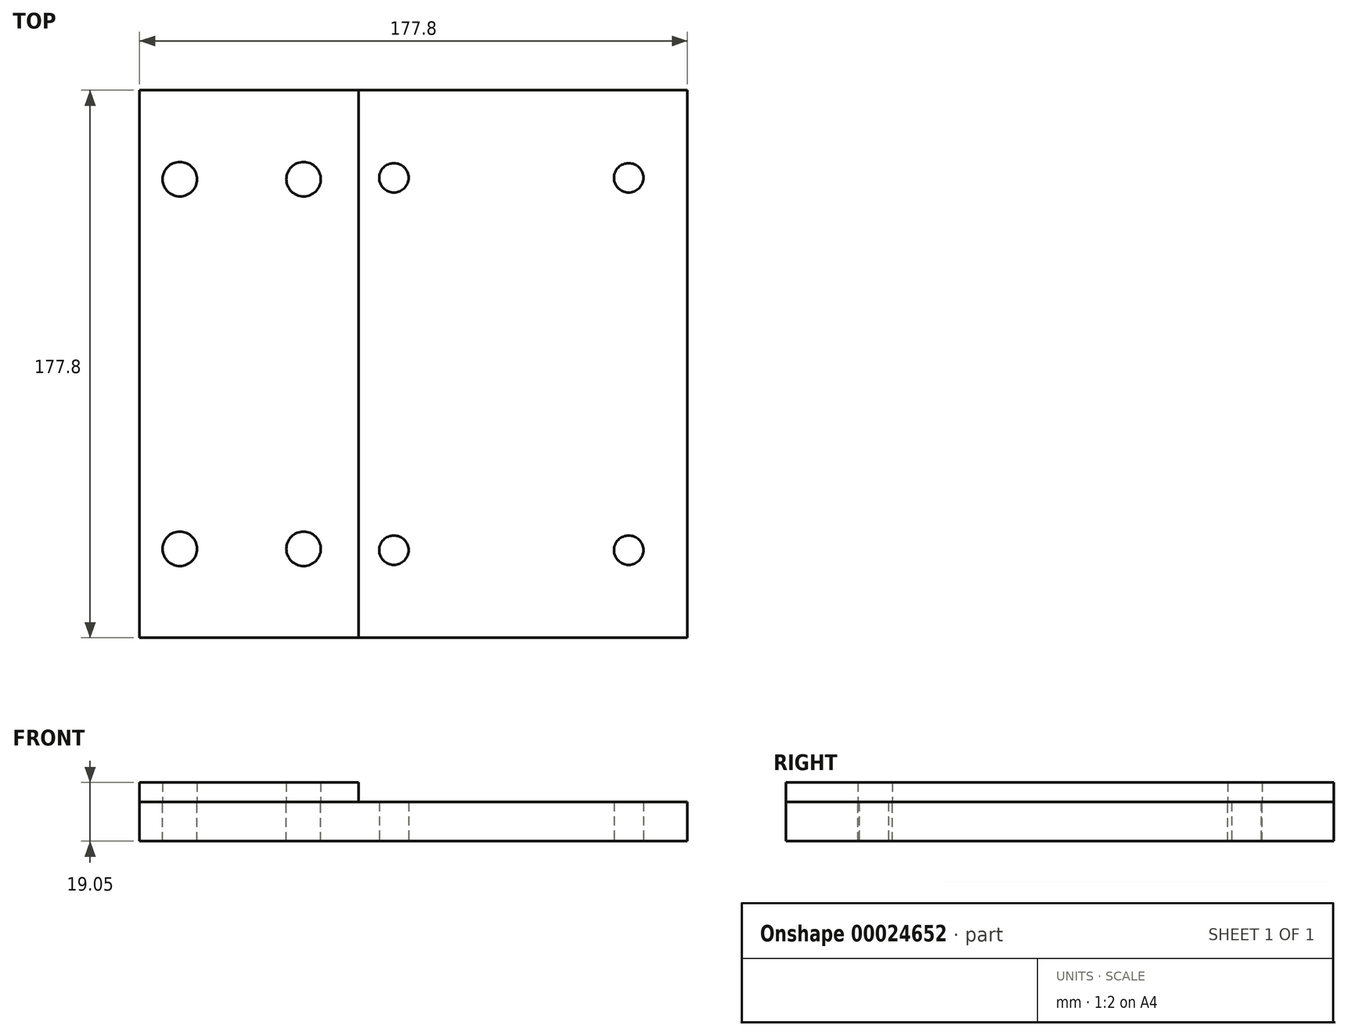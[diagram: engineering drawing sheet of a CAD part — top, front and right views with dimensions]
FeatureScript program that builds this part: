
annotation { "Feature Type Name" : "Feature", "Feature Type Description" : "" }
export const myFeature = defineFeature(function(context is Context, id is Id, definition is map)
    precondition{}
    {
        {
            var Q0;
            Q0=qCreatedBy(makeId("Top.planeOp"),FACE);
            var sketch = newSketch(context, id + "F0", { "sketchPlane" : qUnion([Q0])});
            skLineSegment(sketch, "E0.rect.bottom", {"start": v(-88.9, 88.9) * mm, "end": v(88.9, 88.9) * mm});
            skLineSegment(sketch, "E0.rect.top", {"start": v(-88.9, -88.9) * mm, "end": v(88.9, -88.9) * mm});
            skLineSegment(sketch, "E0.rect.left", {"start": v(-88.9, 88.9) * mm, "end": v(-88.9, -88.9) * mm});
            skLineSegment(sketch, "E0.rect.right", {"start": v(88.9, 88.9) * mm, "end": v(88.9, -88.9) * mm});
            skPoint(sketch, "E0.rect.middle", {"position": v(0, 0) * mm});
            skLineSegment(sketch, "E1.0", {"start": v(31.75, 88.9) * mm, "end": v(31.75, -88.9) * mm, "construction": true});
            skLineSegment(sketch, "E2.0", {"start": v(69.85, 88.9) * mm, "end": v(69.85, -88.9) * mm, "construction": true});
            skLineSegment(sketch, "E3", {"start": v(0, 0) * mm, "end": v(100.51, 0) * mm, "construction": true});
            skLineSegment(sketch, "E4.0", {"start": v(0, 60.45) * mm, "end": v(100.51, 60.45) * mm, "construction": true});
            skCircle(sketch, "E5", {"center": v(69.85, 60.45) * mm, "radius": 4.76 * mm});
            skCircle(sketch, "E6.MirrorC", {"center": v(-6.35, 60.45) * mm, "radius": 4.76 * mm});
            skCircle(sketch, "E7.MirrorC", {"center": v(-6.35, -60.45) * mm, "radius": 4.76 * mm});
            skCircle(sketch, "E8.MirrorC", {"center": v(69.85, -60.45) * mm, "radius": 4.76 * mm});
            skSolve(sketch);
        }
        {
            var Q0;
            Q0=makeQuery(id+"F0.imprint","IMPRINT",FACE,{"disambiguationData":[TD([[makeQuery(id+"F0.imprint","IMPRINT",EDGE,{"derivedFrom":sQuery(id+"F0.wireOp",EDGE,"E0.rect.bottom")}),-1.0]])]});
            extrude(context, id + "F1", {"entities" : qUnion([Q0]), "depth" : 12.7 * mm});
        }
        {
            var Q0;
            Q0=makeQuery(id+"F1.opExtrude","CAP_FACE",FACE,{"disambiguationData":[OSD([sQuery(id+"F0.wireOp",EDGE,"E0.rect.bottom"),sQuery(id+"F0.wireOp",EDGE,"E0.rect.top"),sQuery(id+"F0.wireOp",EDGE,"E0.rect.left"),sQuery(id+"F0.wireOp",EDGE,"E0.rect.right"),sQuery(id+"F0.wireOp",EDGE,"E5"),sQuery(id+"F0.wireOp",EDGE,"E6.MirrorC"),sQuery(id+"F0.wireOp",EDGE,"E7.MirrorC"),sQuery(id+"F0.wireOp",EDGE,"E8.MirrorC")])],"isStart":false});
            var sketch = newSketch(context, id + "F2", { "sketchPlane" : qUnion([Q0])});
            skLineSegment(sketch, "E9", {"start": v(-88.9, 0) * mm, "end": v(102.79, 0) * mm, "construction": true});
            skLineSegment(sketch, "E10", {"start": v(-88.9, 88.9) * mm, "end": v(-88.9, -109.74) * mm, "construction": true});
            skLineSegment(sketch, "E11.0", {"start": v(-75.84, 88.9) * mm, "end": v(-75.84, -109.74) * mm, "construction": true});
            skLineSegment(sketch, "E12.0", {"start": v(-35.66, 88.9) * mm, "end": v(-35.66, -109.74) * mm, "construction": true});
            skLineSegment(sketch, "E13.0", {"start": v(-88.9, -60) * mm, "end": v(102.79, -60) * mm, "construction": true});
            skPoint(sketch, "E14", {"position": v(-75.84, -60) * mm});
            skPoint(sketch, "E15", {"position": v(-35.66, -60) * mm});
            skPoint(sketch, "E16.MirrorP", {"position": v(-75.84, 60) * mm});
            skPoint(sketch, "E17.MirrorP", {"position": v(-35.66, 60) * mm});
            skSolve(sketch);
        }
        {
            var Q0;
            Q0=sQuery(id+"F2.wireOp",VERTEX,"E16.MirrorP");
            var Q1;
            Q1=sQuery(id+"F2.wireOp",VERTEX,"E17.MirrorP");
            var Q2;
            Q2=sQuery(id+"F2.wireOp",VERTEX,"E14");
            var Q3;
            Q3=sQuery(id+"F2.wireOp",VERTEX,"E15");
            var Q4;
            Q4=makeQuery(id+"F1.opExtrude","SWEPT_BODY",BODY,{"disambiguationData":[OSD([sQuery(id+"F0.wireOp",EDGE,"E0.rect.bottom"),sQuery(id+"F0.wireOp",EDGE,"E0.rect.top"),sQuery(id+"F0.wireOp",EDGE,"E0.rect.left"),sQuery(id+"F0.wireOp",EDGE,"E0.rect.right"),sQuery(id+"F0.wireOp",EDGE,"E5"),sQuery(id+"F0.wireOp",EDGE,"E6.MirrorC"),sQuery(id+"F0.wireOp",EDGE,"E7.MirrorC"),sQuery(id+"F0.wireOp",EDGE,"E8.MirrorC")])]});
            hole(context, id + "F3", {"style" : HoleStyle.SIMPLE, "holeDiameter" : 11.18 * mm, "endStyle" : HoleEndStyle.THROUGH, "locations" : qUnion([Q0, Q1, Q2, Q3]), "scope" : qUnion([Q4])});
        }
        {
            var Q0;
            Q0=makeQuery(id+"F1.opExtrude","CAP_FACE",FACE,{"disambiguationData":[OSD([sQuery(id+"F0.wireOp",EDGE,"E0.rect.bottom"),sQuery(id+"F0.wireOp",EDGE,"E0.rect.top"),sQuery(id+"F0.wireOp",EDGE,"E0.rect.left"),sQuery(id+"F0.wireOp",EDGE,"E0.rect.right"),sQuery(id+"F0.wireOp",EDGE,"E5"),sQuery(id+"F0.wireOp",EDGE,"E6.MirrorC"),sQuery(id+"F0.wireOp",EDGE,"E7.MirrorC"),sQuery(id+"F0.wireOp",EDGE,"E8.MirrorC")])],"isStart":false});
            var sketch = newSketch(context, id + "F4", { "sketchPlane" : qUnion([Q0])});
            skLineSegment(sketch, "E18.0", {"start": v(-88.9, 88.9) * mm, "end": v(88.9, 88.9) * mm});
            skCircle(sketch, "E19.0", {"center": v(-75.84, 60) * mm, "radius": 5.59 * mm});
            skCircle(sketch, "E20.0", {"center": v(-35.66, 60) * mm, "radius": 5.59 * mm});
            skCircle(sketch, "E21.0", {"center": v(-35.66, -60) * mm, "radius": 5.59 * mm});
            skCircle(sketch, "E22.0", {"center": v(-75.84, -60) * mm, "radius": 5.59 * mm});
            skLineSegment(sketch, "E23.0", {"start": v(-88.9, 88.9) * mm, "end": v(-88.9, -88.9) * mm});
            skLineSegment(sketch, "E24.0", {"start": v(-88.9, -88.9) * mm, "end": v(88.9, -88.9) * mm});
            skLineSegment(sketch, "E25.0", {"start": v(-17.78, 88.9) * mm, "end": v(-17.78, -88.9) * mm});
            skSolve(sketch);
        }
        {
            var Q0;
            Q0 = qSketchRegion(id + "F4", true);
            extrude(context, id + "F5", {"entities" : qUnion([Q0]), "depth" : 6.35 * mm});
        }
    });
